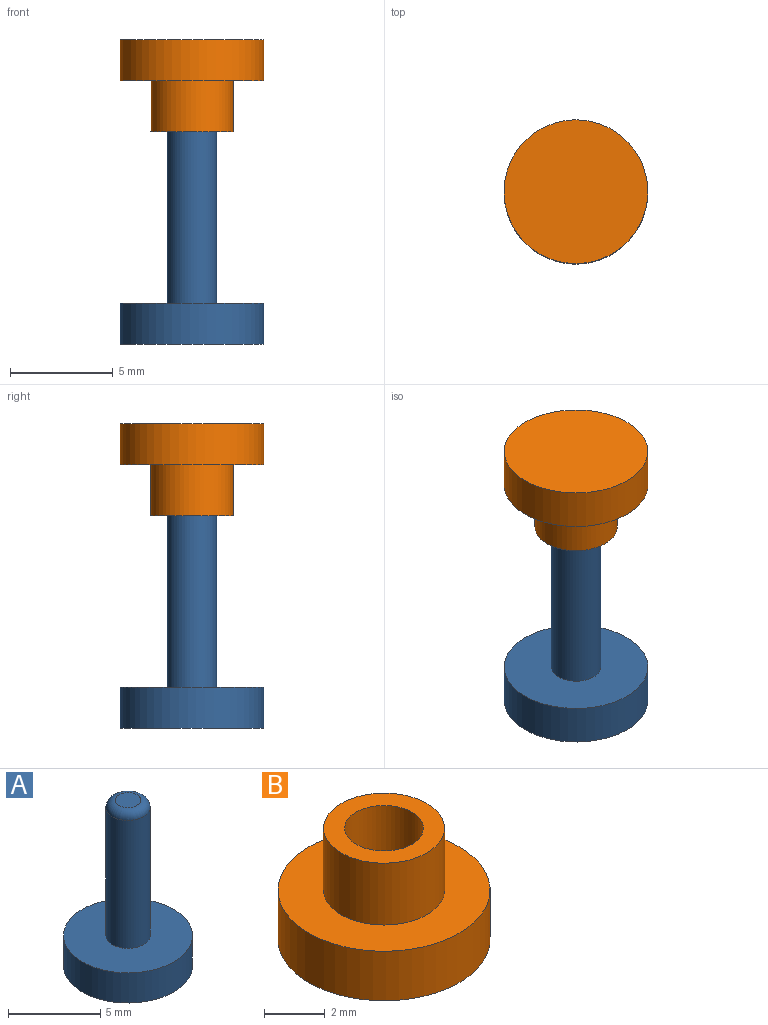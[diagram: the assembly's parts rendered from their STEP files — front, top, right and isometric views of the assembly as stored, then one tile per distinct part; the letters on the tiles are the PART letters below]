
ASSEMBLY  parts=2 mates=1
PART A: 6 faces, bbox 7x7x11 mm
  f0: cylinder r=3.5mm len=7mm, axis (0,0,-1), area 44mm2, adj f1,f2
  f1: plane 7x7mm, normal (0,0,1), area 34mm2, adj f0,f3
  f2: plane 7x7mm, normal (0,0,-1), area 38.5mm2, adj f0
  f3: cylinder r=1.2mm len=8.5mm, axis (0,0,-1), area 64.1mm2, adj f1,f5
  f4: plane 1.4x1.4mm, normal (0,0,1), area 1.5mm2, adj f5
  f5: torus R=0.7mm, axis (0,0,1), area 5mm2, adj f3,f4
PART B: 7 faces, bbox 7x7x4.5 mm
  f0: cylinder r=3.5mm len=7mm, axis (0,0,1), area 44mm2, adj f1,f2
  f1: plane 7x7mm, normal (0,0,-1), area 38.5mm2, adj f0
  f2: plane 7x7mm, normal (0,0,1), area 25.9mm2, adj f0,f3
  f3: cylinder r=2mm len=4mm, axis (0,0,-1), area 31.4mm2, adj f2,f4
  f4: plane 4x4mm, normal (0,0,1), area 7.3mm2, adj f3,f5
  f5: cylinder r=1.3mm len=4mm, axis (0,0,1), area 32.7mm2, adj f4,f6
  f6: plane 2.6x2.6mm, normal (0,0,1), area 5.3mm2, adj f5
PLACE A t=(-8.19,-4.96,5.2)mm
PLACE B rot(axis=(1,0,0),180deg) t=(-8.19,11.64,20.04)mm
MATE slider B.f0 <-> A.f3  axis (0,0,-1) through (-8.19,-4.96,15.54)mm
